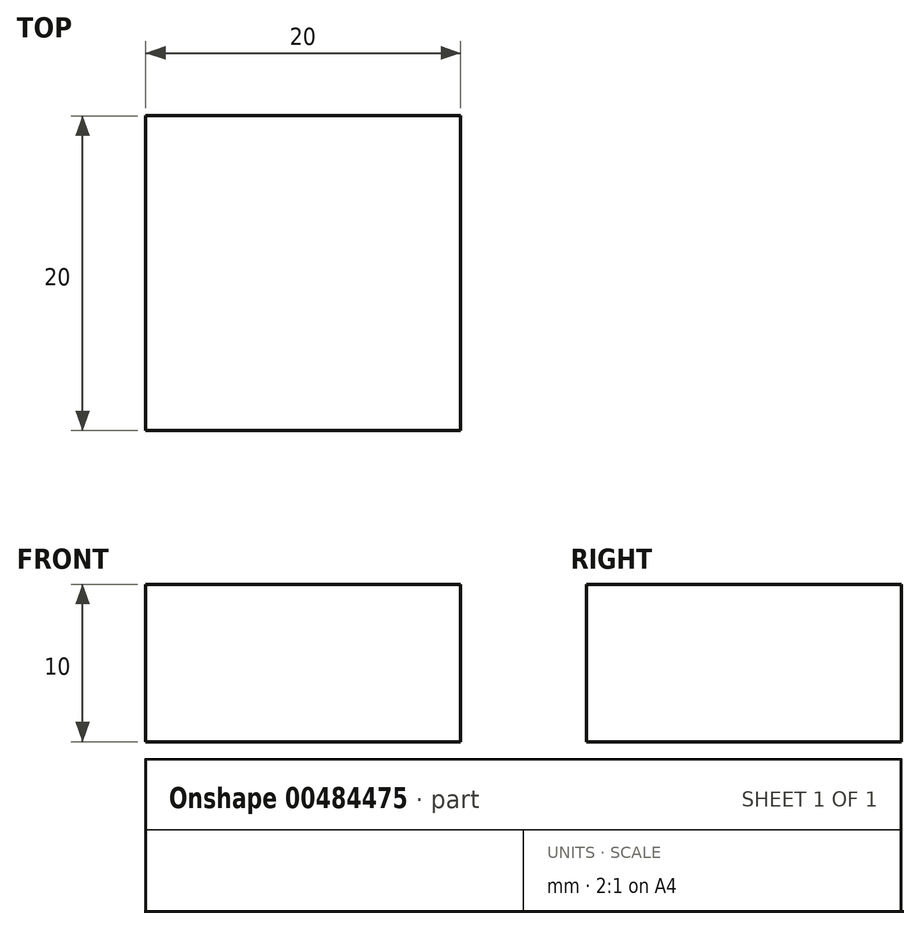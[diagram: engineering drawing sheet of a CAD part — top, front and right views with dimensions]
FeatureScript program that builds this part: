
annotation { "Feature Type Name" : "Feature", "Feature Type Description" : "" }
export const myFeature = defineFeature(function(context is Context, id is Id, definition is map)
    precondition{}
    {
        {
            var Q0;
            Q0=qCreatedBy(makeId("Top.planeOp"),FACE);
            var sketch = newSketch(context, id + "F0", { "sketchPlane" : qUnion([Q0])});
            skLineSegment(sketch, "E0.bottom", {"start": v(-104.26, -57.4) * mm, "end": v(-84.26, -57.4) * mm});
            skLineSegment(sketch, "E0.top", {"start": v(-104.26, -77.4) * mm, "end": v(-84.26, -77.4) * mm});
            skLineSegment(sketch, "E0.left", {"start": v(-104.26, -57.4) * mm, "end": v(-104.26, -77.4) * mm});
            skLineSegment(sketch, "E0.right", {"start": v(-84.26, -57.4) * mm, "end": v(-84.26, -77.4) * mm});
            skSolve(sketch);
        }
        {
            var Q0;
            Q0=makeQuery(id+"F0.imprint","IMPRINT",FACE,{"disambiguationData":[TD([[makeQuery(id+"F0.imprint","IMPRINT",EDGE,{"derivedFrom":sQuery(id+"F0.wireOp",EDGE,"E0.bottom")}),-1.0]])]});
            extrude(context, id + "F1", {"entities" : qUnion([Q0]), "depth" : 10 * mm});
        }
    });
